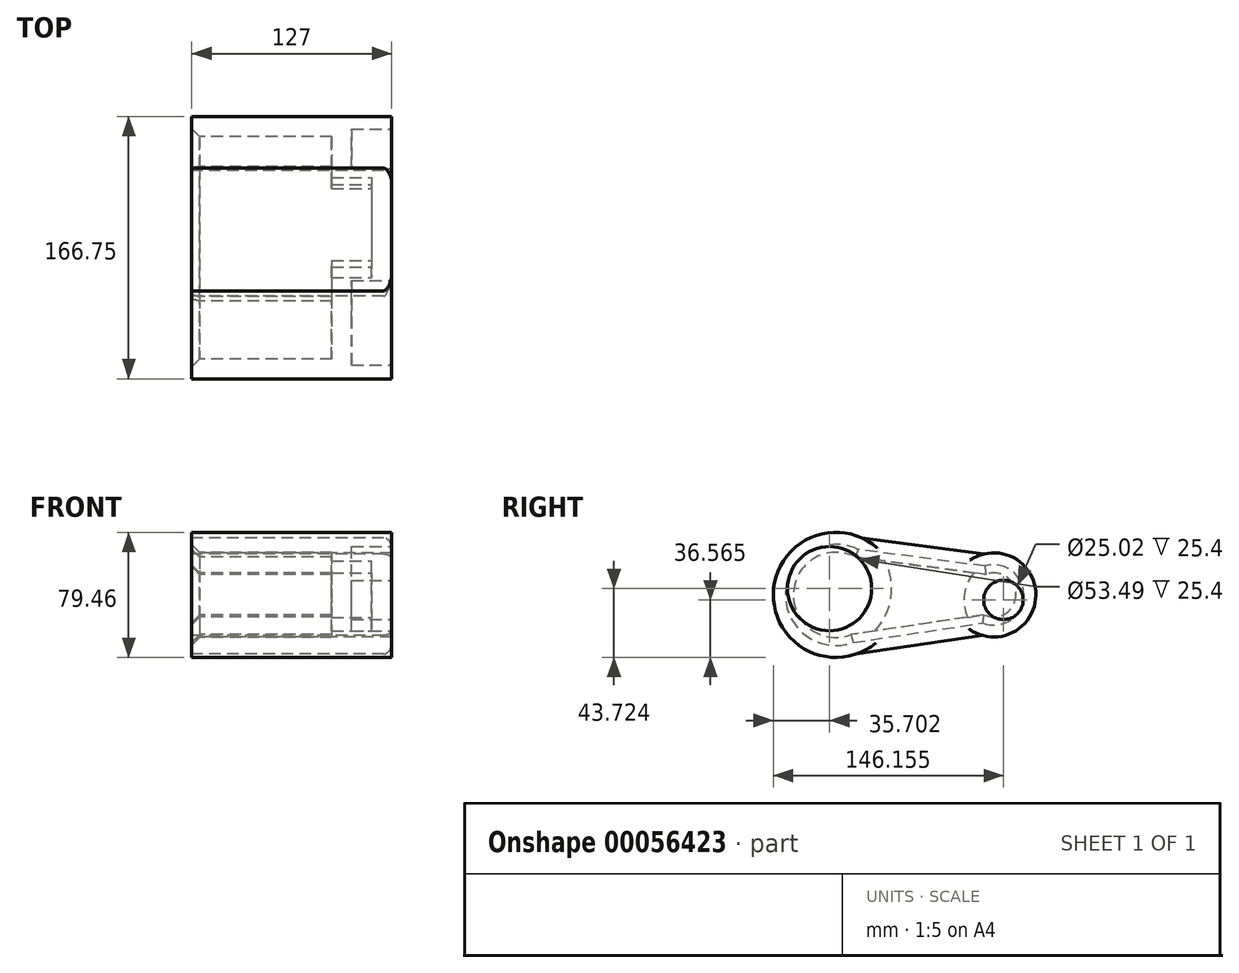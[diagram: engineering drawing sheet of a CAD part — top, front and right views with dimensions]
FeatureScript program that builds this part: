
annotation { "Feature Type Name" : "Feature", "Feature Type Description" : "" }
export const myFeature = defineFeature(function(context is Context, id is Id, definition is map)
    precondition{}
    {
        {
            var Q0;
            Q0=qCreatedBy(makeId("Right.planeOp"),FACE);
            var sketch = newSketch(context, id + "F0", { "sketchPlane" : qUnion([Q0])});
            skCircle(sketch, "E0", {"center": v(0, 0) * mm, "radius": 39.73 * mm});
            skCircle(sketch, "E1", {"center": v(100.27, 0) * mm, "radius": 26.74 * mm});
            skLineSegment(sketch, "E2", {"start": v(16.16, 36.3) * mm, "end": v(94.18, 26.04) * mm});
            skLineSegment(sketch, "E3", {"start": v(12.75, -37.63) * mm, "end": v(92.73, -25.66) * mm});
            skSolve(sketch);
        }
        {
            var Q0;
            {var subQ0=sQuery(id+"F0.wireOp",EDGE,"E0");var subQ1=makeQuery(id+"F0.imprint","INTERSECT",VERTEX,{"derivedFrom":[subQ0,sQuery(id+"F0.wireOp",EDGE,"E2")]});Q0=makeQuery(id+"F0.imprint","IMPRINT",FACE,{"disambiguationData":[TD([[makeQuery(id+"F0.imprint","IMPRINT",EDGE,{"disambiguationData":[TD([[subQ1,-1.0]])],"derivedFrom":subQ0}),1.0]])]});}
            var Q1;
            {var subQ0=sQuery(id+"F0.wireOp",EDGE,"E2");Q1=makeQuery(id+"F0.imprint","IMPRINT",FACE,{"disambiguationData":[TD([[makeQuery(id+"F0.imprint","IMPRINT",EDGE,{"derivedFrom":subQ0}),-1.0]])]});}
            var Q2;
            {var subQ0=sQuery(id+"F0.wireOp",EDGE,"E1");var subQ1=makeQuery(id+"F0.imprint","INTERSECT",VERTEX,{"derivedFrom":[subQ0,sQuery(id+"F0.wireOp",EDGE,"E2")]});Q2=makeQuery(id+"F0.imprint","IMPRINT",FACE,{"disambiguationData":[TD([[makeQuery(id+"F0.imprint","IMPRINT",EDGE,{"disambiguationData":[TD([[subQ1,-1.0]])],"derivedFrom":subQ0}),1.0]])]});}
            extrude(context, id + "F1", {"entities" : qUnion([Q0, Q1, Q2]), "depth" : 127 * mm});
        }
        {
            var Q0;
            Q0=makeQuery(id+"F1.opExtrude","CAP_FACE",FACE,{"disambiguationData":[OSD([sQuery(id+"F0.wireOp",EDGE,"E0"),sQuery(id+"F0.wireOp",EDGE,"E1"),sQuery(id+"F0.wireOp",EDGE,"E2"),sQuery(id+"F0.wireOp",EDGE,"E3")])],"isStart":false});
            var sketch = newSketch(context, id + "F2", { "sketchPlane" : qUnion([Q0])});
            skCircle(sketch, "E4", {"center": v(-4.03, 4) * mm, "radius": 26.74 * mm});
            skCircle(sketch, "E5", {"center": v(106.43, -3.16) * mm, "radius": 12.51 * mm});
            skSolve(sketch);
        }
        {
            var Q0;
            Q0=makeQuery(id+"F2.imprint","IMPRINT",FACE,{"disambiguationData":[TD([[makeQuery(id+"F2.imprint","IMPRINT",EDGE,{"derivedFrom":sQuery(id+"F2.wireOp",EDGE,"E4")}),1.0]])]});
            var Q1;
            Q1=makeQuery(id+"F2.imprint","IMPRINT",FACE,{"disambiguationData":[TD([[makeQuery(id+"F2.imprint","IMPRINT",EDGE,{"derivedFrom":sQuery(id+"F2.wireOp",EDGE,"E5")}),1.0]])]});
            extrude(context, id + "F3", {"entities" : qUnion([Q0, Q1]), "operationType" : NewBodyOperationType.REMOVE, "oppositeDirection" : true, "depth" : 25.4 * mm});
        }
        {
            var Q0;
            Q0=makeQuery(id+"F3.boolean.opBoolean","COPY",EDGE,{"derivedFrom":makeQuery(id+"F3.opExtrude","CAP_EDGE",EDGE,{"disambiguationData":[OSD([sQuery(id+"F2.wireOp",EDGE,"E4")])],"isStart":true})});
            var Q1;
            Q1=makeQuery(id+"F3.boolean.opBoolean","COPY",EDGE,{"derivedFrom":makeQuery(id+"F3.opExtrude","CAP_EDGE",EDGE,{"disambiguationData":[OSD([sQuery(id+"F2.wireOp",EDGE,"E5")])],"isStart":true})});
            var Q2;
            Q2=makeQuery(id+"F1.opExtrude","CAP_EDGE",EDGE,{"disambiguationData":[OSD([sQuery(id+"F0.wireOp",EDGE,"E2")])],"isStart":false});
            var Q3;
            Q3=makeQuery(id+"F1.opExtrude","CAP_EDGE",EDGE,{"disambiguationData":[OSD([sQuery(id+"F0.wireOp",EDGE,"E3")])],"isStart":false});
            fillet(context, id + "F4", {"entities" : qUnion([Q0, Q1, Q2, Q3]), "radius" : 5.08 * mm, "tangentPropagation" : true, "allowEdgeOverflow" : false});
        }
        {
            var Q0;
            Q0=makeQuery(id+"F1.opExtrude","CAP_FACE",FACE,{"disambiguationData":[OSD([sQuery(id+"F0.wireOp",EDGE,"E0"),sQuery(id+"F0.wireOp",EDGE,"E1"),sQuery(id+"F0.wireOp",EDGE,"E2"),sQuery(id+"F0.wireOp",EDGE,"E3")])],"isStart":true});
            shell(context, id + "F5", {"entities" : qUnion([Q0]), "thickness" : 12.7 * mm});
        }
        {
            var Q0;
            Q0=makeQuery(id+"F5.opShell","OFFSET_EDGE",EDGE,{"disambiguationData":[OSD([sQuery(id+"F0.wireOp",EDGE,"E3")])]});
            var Q1;
            Q1=makeQuery(id+"F5.opShell","OFFSET_EDGE",EDGE,{"disambiguationData":[OSD([sQuery(id+"F0.wireOp",EDGE,"E1")])]});
            var Q2;
            Q2=makeQuery(id+"F5.opShell","OFFSET_EDGE",EDGE,{"disambiguationData":[OSD([sQuery(id+"F0.wireOp",EDGE,"E2")])]});
            var Q3;
            Q3=makeQuery(id+"F5.opShell","OFFSET_EDGE",EDGE,{"disambiguationData":[OSD([sQuery(id+"F0.wireOp",EDGE,"E0")])]});
            chamfer(context, id + "F6", {"entities" : qUnion([Q0, Q1, Q2, Q3]), "width" : 5.08 * mm, "tangentPropagation" : true});
        }
    });
